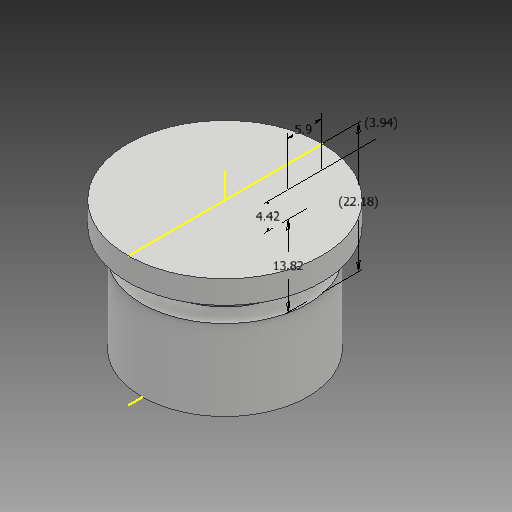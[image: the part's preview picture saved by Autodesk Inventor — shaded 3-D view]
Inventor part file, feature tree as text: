
AUTODESK INVENTOR PART (.ipt)
format: ipt  version: 2019.2 (Build 232265000, 265)  size: 115,712 bytes
history: native  units: mm
features: sketch x2, extrude x1, revolve x1
ambient origin geometry x8: Origin, YZ Plane, XZ Plane, XY Plane, X Axis, Y Axis, Z Axis, Center Point
bodies: Solid1 (feature_tree)
feature tree (4):
  extrude  "Extrusion1"  Depth=22.18mm TaperAngle=0.0deg
  revolve  "Revolution1"  [1 undecoded]
  sketch  "Sketch1"  dims[d0=33.3mm d1=22.18mm d2=0.0mm]
  sketch  "Sketch2"  dims[d3=13.82mm d4=4.42mm d5=5.9mm d6=90.0deg d7=22.18mm d8=3.94mm]
note: 1 required parameter value undecoded (feature->parameter linkage not recoverable at this tier; creation-order binding heuristic only, values carry confidence <= 0.55)
